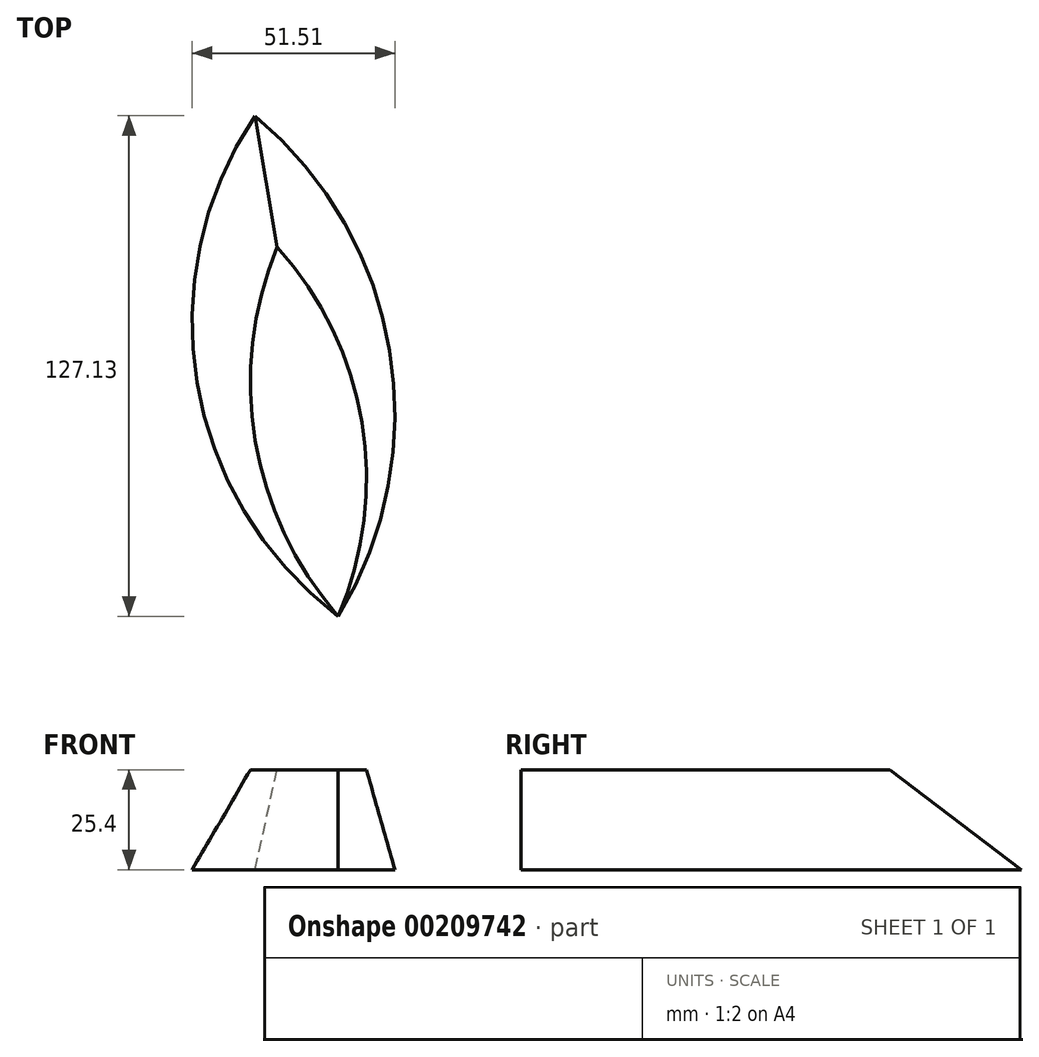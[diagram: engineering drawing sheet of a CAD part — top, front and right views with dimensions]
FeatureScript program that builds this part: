
annotation { "Feature Type Name" : "Feature", "Feature Type Description" : "" }
export const myFeature = defineFeature(function(context is Context, id is Id, definition is map)
    precondition{}
    {
        {
            var Q0;
            Q0=qCreatedBy(makeId("Top.planeOp"),FACE);
            var sketch = newSketch(context, id + "F0", { "sketchPlane" : qUnion([Q0])});
            skArc(sketch, "E0", {"start": v(-21.1, 127.13) * mm, "mid": v(-35.83, 59.37) * mm, "end": v(0, 0) * mm});
            skArc(sketch, "E1", {"start": v(0, 0) * mm, "mid": v(13.08, 67.49) * mm, "end": v(-21.1, 127.13) * mm});
            skSolve(sketch);
        }
        {
            var Q0;
            Q0=qCreatedBy(makeId("Top.planeOp"),FACE);
            cPlane(context, id + "F1", {"entities" : qUnion([Q0]), "cplaneType" : CPlaneType.OFFSET, "offset" : 25.4 * mm, "width" : 152.4 * mm, "height" : 152.4 * mm});
        }
        {
            var Q0;
            Q0=qCreatedBy(id+"F1.planeOp",FACE);
            var sketch = newSketch(context, id + "F2", { "sketchPlane" : qUnion([Q0])});
            skArc(sketch, "E2", {"start": v(-15.52, 93.8) * mm, "mid": v(-21.1, 44.69) * mm, "end": v(0, 0) * mm});
            skArc(sketch, "E3", {"start": v(0, 0) * mm, "mid": v(6, 49.17) * mm, "end": v(-15.52, 93.8) * mm});
            skSolve(sketch);
        }
        {
            var Q0;
            Q0=makeQuery(id+"F0.imprint","IMPRINT",FACE,{"disambiguationData":[TD([[makeQuery(id+"F0.imprint","IMPRINT",EDGE,{"derivedFrom":sQuery(id+"F0.wireOp",EDGE,"E0")}),1.0]])]});
            var Q1;
            Q1=makeQuery(id+"F2.imprint","IMPRINT",FACE,{"disambiguationData":[TD([[makeQuery(id+"F2.imprint","IMPRINT",EDGE,{"derivedFrom":sQuery(id+"F2.wireOp",EDGE,"E2")}),1.0]])]});
            loft(context, id + "F3", {"sheetProfilesArray" : [{ "sheetProfileEntities" : qUnion([Q0]) }, { "sheetProfileEntities" : qUnion([Q1]) }]});
        }
    });
